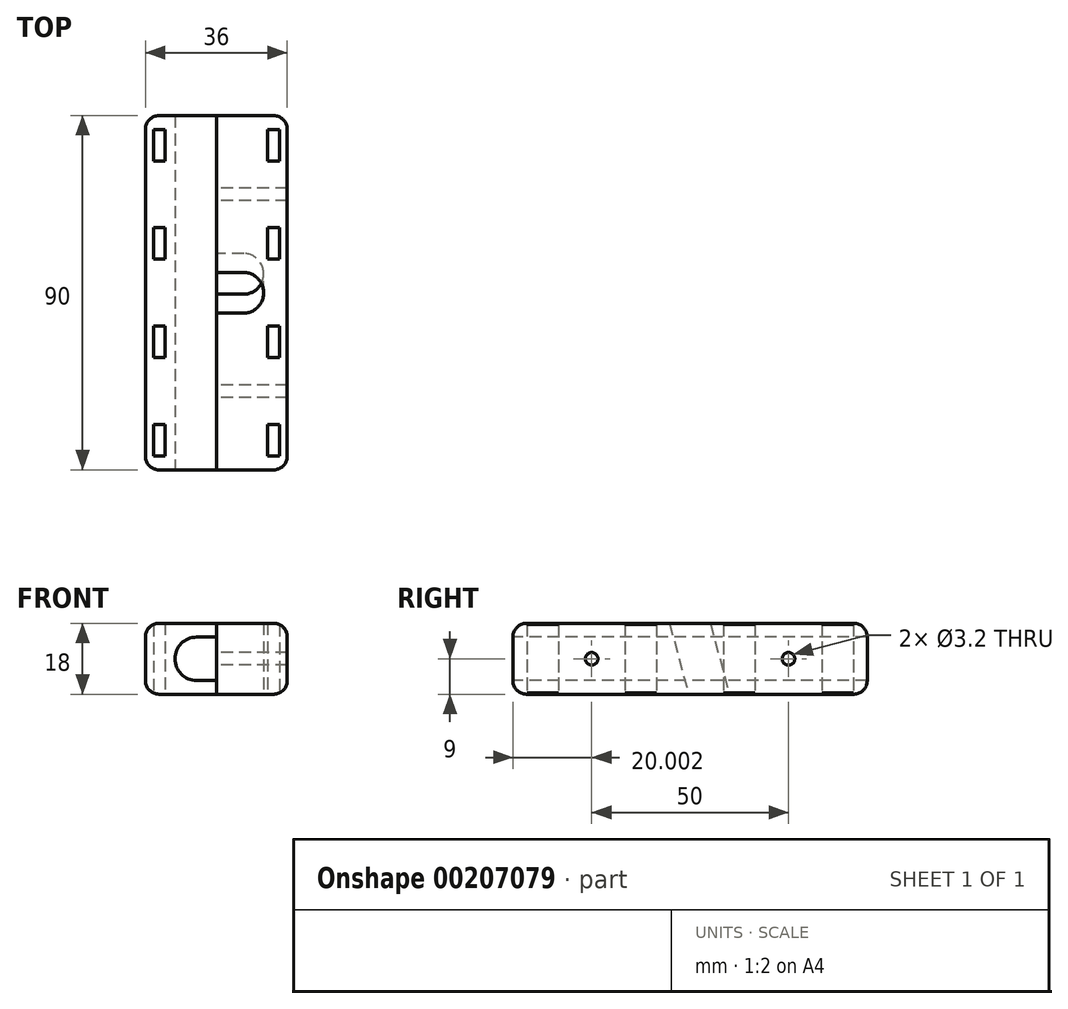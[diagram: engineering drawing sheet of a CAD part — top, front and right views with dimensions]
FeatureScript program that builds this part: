
annotation { "Feature Type Name" : "Feature", "Feature Type Description" : "" }
export const myFeature = defineFeature(function(context is Context, id is Id, definition is map)
    precondition{}
    {
        {
            var Q0;
            Q0=qCreatedBy(makeId("Top.planeOp"),FACE);
            var sketch = newSketch(context, id + "F0", { "sketchPlane" : qUnion([Q0])});
            skLineSegment(sketch, "E0.bottom", {"start": v(1.07, -6.1) * mm, "end": v(19.07, -6.1) * mm});
            skLineSegment(sketch, "E0.top", {"start": v(1.07, 83.9) * mm, "end": v(19.07, 83.9) * mm});
            skLineSegment(sketch, "E0.left", {"start": v(1.07, -6.1) * mm, "end": v(1.07, 83.9) * mm});
            skLineSegment(sketch, "E0.right", {"start": v(19.07, -6.1) * mm, "end": v(19.07, 83.9) * mm});
            skLineSegment(sketch, "E1.bottom", {"start": v(3.07, 80.4) * mm, "end": v(6.07, 80.4) * mm});
            skLineSegment(sketch, "E1.top", {"start": v(3.07, 72.4) * mm, "end": v(6.07, 72.4) * mm});
            skLineSegment(sketch, "E1.left", {"start": v(3.07, 80.4) * mm, "end": v(3.07, 72.4) * mm});
            skLineSegment(sketch, "E1.right", {"start": v(6.07, 80.4) * mm, "end": v(6.07, 72.4) * mm});
            skLineSegment(sketch, "E2.0.1.0", {"start": v(6.07, 55.4) * mm, "end": v(6.07, 47.4) * mm});
            skLineSegment(sketch, "E2.0.1.1", {"start": v(3.07, 55.4) * mm, "end": v(3.07, 47.4) * mm});
            skLineSegment(sketch, "E2.0.1.2", {"start": v(3.07, 47.4) * mm, "end": v(6.07, 47.4) * mm});
            skLineSegment(sketch, "E2.0.1.3", {"start": v(3.07, 55.4) * mm, "end": v(6.07, 55.4) * mm});
            skLineSegment(sketch, "E2.0.2.0", {"start": v(6.07, 30.4) * mm, "end": v(6.07, 22.4) * mm});
            skLineSegment(sketch, "E2.0.2.1", {"start": v(3.07, 30.4) * mm, "end": v(3.07, 22.4) * mm});
            skLineSegment(sketch, "E2.0.2.2", {"start": v(3.07, 22.4) * mm, "end": v(6.07, 22.4) * mm});
            skLineSegment(sketch, "E2.0.2.3", {"start": v(3.07, 30.4) * mm, "end": v(6.07, 30.4) * mm});
            skLineSegment(sketch, "E2.0.3.0", {"start": v(6.07, 5.4) * mm, "end": v(6.07, -2.6) * mm});
            skLineSegment(sketch, "E2.0.3.1", {"start": v(3.07, 5.4) * mm, "end": v(3.07, -2.6) * mm});
            skLineSegment(sketch, "E2.0.3.2", {"start": v(3.07, -2.6) * mm, "end": v(6.07, -2.6) * mm});
            skLineSegment(sketch, "E2.0.3.3", {"start": v(3.07, 5.4) * mm, "end": v(6.07, 5.4) * mm});
            skLineSegment(sketch, "E2.direction1", {"start": v(3.07, 72.4) * mm, "end": v(28.07, 72.4) * mm, "construction": true});
            skLineSegment(sketch, "E2.direction2", {"start": v(3.07, 72.4) * mm, "end": v(3.07, 47.4) * mm, "construction": true});
            skLineSegment(sketch, "E3", {"start": v(6.07, 80.4) * mm, "end": v(6.07, 83.9) * mm, "construction": true});
            skLineSegment(sketch, "E4", {"start": v(6.07, -2.6) * mm, "end": v(6.07, -6.1) * mm, "construction": true});
            skSolve(sketch);
        }
        {
            var Q0;
            Q0 = qSketchRegion(id + "F0", true);
            extrude(context, id + "F1", {"entities" : qUnion([Q0]), "depth" : 18 * mm});
        }
        {
            var Q0;
            Q0=makeQuery(id+"F1.opExtrude","SWEPT_FACE",FACE,{"disambiguationData":[OSD([sQuery(id+"F0.wireOp",EDGE,"E0.bottom")])]});
            var sketch = newSketch(context, id + "F2", { "sketchPlane" : qUnion([Q0])});
            skArc(sketch, "E5", {"start": v(19.07, 11.24) * mm, "mid": v(8.55, 9) * mm, "end": v(19.07, 6.76) * mm});
            skPoint(sketch, "E5.centerSnap0", {"position": v(19.07, 9) * mm});
            skLineSegment(sketch, "E6.bottom", {"start": v(14.05, 3.5) * mm, "end": v(19.07, 3.5) * mm});
            skLineSegment(sketch, "E6.top", {"start": v(14.05, 14.5) * mm, "end": v(19.07, 14.5) * mm});
            skLineSegment(sketch, "E6.left", {"start": v(14.05, 3.5) * mm, "end": v(14.05, 14.5) * mm});
            skLineSegment(sketch, "E6.right", {"start": v(19.07, 3.5) * mm, "end": v(19.07, 14.5) * mm});
            skSolve(sketch);
        }
        {
            var Q0;
            Q0=makeQuery(id+"F1.opExtrude","CAP_EDGE",EDGE,{"disambiguationData":[OSD([sQuery(id+"F0.wireOp",EDGE,"E0.bottom")])],"isStart":false});
            var Q1;
            Q1=makeQuery(id+"F1.opExtrude","CAP_EDGE",EDGE,{"disambiguationData":[OSD([sQuery(id+"F0.wireOp",EDGE,"E0.left")])],"isStart":false});
            var Q2;
            Q2=makeQuery(id+"F1.opExtrude","SWEPT_EDGE",EDGE,{"disambiguationData":[OSD([sQuery(id+"F0.wireOp",EDGE,"E0.bottom"),sQuery(id+"F0.wireOp",EDGE,"E0.left")])]});
            var Q3;
            Q3=makeQuery(id+"F1.opExtrude","CAP_EDGE",EDGE,{"disambiguationData":[OSD([sQuery(id+"F0.wireOp",EDGE,"E0.bottom")])],"isStart":true});
            var Q4;
            Q4=makeQuery(id+"F1.opExtrude","CAP_EDGE",EDGE,{"disambiguationData":[OSD([sQuery(id+"F0.wireOp",EDGE,"E0.left")])],"isStart":true});
            var Q5;
            Q5=makeQuery(id+"F1.opExtrude","SWEPT_EDGE",EDGE,{"disambiguationData":[OSD([sQuery(id+"F0.wireOp",EDGE,"E0.top"),sQuery(id+"F0.wireOp",EDGE,"E0.left")])]});
            var Q6;
            Q6=makeQuery(id+"F1.opExtrude","CAP_EDGE",EDGE,{"disambiguationData":[OSD([sQuery(id+"F0.wireOp",EDGE,"E0.top")])],"isStart":false});
            var Q7;
            Q7=makeQuery(id+"F1.opExtrude","CAP_EDGE",EDGE,{"disambiguationData":[OSD([sQuery(id+"F0.wireOp",EDGE,"E0.top")])],"isStart":true});
            fillet(context, id + "F3", {"entities" : qUnion([Q0, Q1, Q2, Q3, Q4, Q5, Q6, Q7]), "radius" : 3.4 * mm, "tangentPropagation" : true, "allowEdgeOverflow" : false});
        }
        {
            var Q0;
            Q0=makeQuery(id+"F1.opExtrude","SWEPT_BODY",BODY,{"disambiguationData":[OSD([sQuery(id+"F0.wireOp",EDGE,"E0.bottom"),sQuery(id+"F0.wireOp",EDGE,"E0.top"),sQuery(id+"F0.wireOp",EDGE,"E0.left"),sQuery(id+"F0.wireOp",EDGE,"E0.right"),sQuery(id+"F0.wireOp",EDGE,"E1.bottom"),sQuery(id+"F0.wireOp",EDGE,"E1.top"),sQuery(id+"F0.wireOp",EDGE,"E1.left"),sQuery(id+"F0.wireOp",EDGE,"E1.right"),sQuery(id+"F0.wireOp",EDGE,"E2.0.1.0"),sQuery(id+"F0.wireOp",EDGE,"E2.0.1.1"),sQuery(id+"F0.wireOp",EDGE,"E2.0.1.2"),sQuery(id+"F0.wireOp",EDGE,"E2.0.1.3"),sQuery(id+"F0.wireOp",EDGE,"E2.0.2.0"),sQuery(id+"F0.wireOp",EDGE,"E2.0.2.1"),sQuery(id+"F0.wireOp",EDGE,"E2.0.2.2"),sQuery(id+"F0.wireOp",EDGE,"E2.0.2.3"),sQuery(id+"F0.wireOp",EDGE,"E2.0.3.0"),sQuery(id+"F0.wireOp",EDGE,"E2.0.3.1"),sQuery(id+"F0.wireOp",EDGE,"E2.0.3.2"),sQuery(id+"F0.wireOp",EDGE,"E2.0.3.3")])]});
            var Q1;
            Q1=makeQuery(id+"F1.opExtrude","SWEPT_FACE",FACE,{"disambiguationData":[OSD([sQuery(id+"F0.wireOp",EDGE,"E0.right")])]});
            mirror(context, id + "F4", {"entities" : qUnion([Q0]), "mirrorPlane" : qUnion([Q1])});
        }
        {
            var Q0;
            Q0 = qSketchRegion(id + "F2", true);
            extrude(context, id + "F5", {"entities" : qUnion([Q0]), "operationType" : NewBodyOperationType.REMOVE, "endBound" : BoundingType.THROUGH_ALL, "oppositeDirection" : true, "depth" : 25 * mm});
        }
        {
            var Q0;
            Q0=makeQuery(id+"F4.opPattern","COPY",FACE,{"derivedFrom":makeQuery(id+"F1.opExtrude","SWEPT_FACE",FACE,{"disambiguationData":[OSD([sQuery(id+"F0.wireOp",EDGE,"E0.right")])]}),"instanceName":"1"});
            var sketch = newSketch(context, id + "F6", { "sketchPlane" : qUnion([Q0])});
            skLineSegment(sketch, "E7", {"start": v(-3.85, -6.17) * mm, "end": v(-45.34, -6.17) * mm, "construction": true});
            skLineSegment(sketch, "E8", {"start": v(-45.34, -6.17) * mm, "end": v(-32.5, 41.73) * mm, "construction": true});
            skLineSegment(sketch, "E9.bottom", {"start": v(-32.97, 20.67) * mm, "end": v(-42.63, 23.26) * mm});
            skLineSegment(sketch, "E9.top", {"start": v(-39.88, -5.09) * mm, "end": v(-49.54, -2.5) * mm});
            skLineSegment(sketch, "E9.left", {"start": v(-32.97, 20.67) * mm, "end": v(-39.88, -5.09) * mm});
            skLineSegment(sketch, "E9.right", {"start": v(-42.63, 23.26) * mm, "end": v(-49.54, -2.5) * mm});
            skLineSegment(sketch, "E10", {"start": v(-37.8, 21.97) * mm, "end": v(-36.5, 26.85) * mm, "construction": true});
            skSolve(sketch);
        }
        {
            var Q0;
            Q0 = qSketchRegion(id + "F6", true);
            extrude(context, id + "F7", {"entities" : qUnion([Q0]), "operationType" : NewBodyOperationType.REMOVE, "oppositeDirection" : true, "depth" : 12 * mm});
        }
        {
            var Q0;
            Q0=makeQuery(id+"F7.boolean.opBoolean","COPY",EDGE,{"derivedFrom":makeQuery(id+"F7.opExtrude","CAP_EDGE",EDGE,{"disambiguationData":[OSD([sQuery(id+"F6.wireOp",EDGE,"E9.right")])],"isStart":false})});
            var Q1;
            Q1=makeQuery(id+"F7.boolean.opBoolean","COPY",EDGE,{"derivedFrom":makeQuery(id+"F7.opExtrude","CAP_EDGE",EDGE,{"disambiguationData":[OSD([sQuery(id+"F6.wireOp",EDGE,"E9.left")])],"isStart":false})});
            fillet(context, id + "F8", {"entities" : qUnion([Q0, Q1]), "radius" : 5 * mm, "tangentPropagation" : true, "allowEdgeOverflow" : false});
        }
        {
            var Q0;
            {var subQ16=sQuery(id+"F0.wireOp",EDGE,"E0.right");var subQ18=sQuery(id+"F0.wireOp",EDGE,"E0.top");Q0=makeQuery(id+"F7.boolean.opBoolean","SPLIT",FACE,{"disambiguationData":[TD([makeQuery(id+"F4.opPattern","COPY",FACE,{"derivedFrom":makeQuery(id+"F1.opExtrude","SWEPT_FACE",FACE,{"disambiguationData":[OSD([subQ18])]}),"instanceName":"1"})])],"derivedFrom":makeQuery(id+"F4.opPattern","COPY",FACE,{"derivedFrom":makeQuery(id+"F1.opExtrude","SWEPT_FACE",FACE,{"disambiguationData":[OSD([subQ16])]}),"instanceName":"1"})});}
            var sketch = newSketch(context, id + "F9", { "sketchPlane" : qUnion([Q0])});
            skCircle(sketch, "E11", {"center": v(-63.9, 9) * mm, "radius": 1.6 * mm});
            skPoint(sketch, "E11.centerSnap0", {"position": v(-83.9, 9) * mm});
            skLineSegment(sketch, "E12", {"start": v(-83.9, 9) * mm, "end": v(-63.9, 9) * mm, "construction": true});
            skCircle(sketch, "E13", {"center": v(-13.9, 9) * mm, "radius": 1.6 * mm});
            skLineSegment(sketch, "E14", {"start": v(-13.9, 9) * mm, "end": v(6.1, 9) * mm, "construction": true});
            skLineSegment(sketch, "E15", {"start": v(-72.4, 13) * mm, "end": v(-55.4, 13) * mm, "construction": true});
            skLineSegment(sketch, "E16", {"start": v(-72.4, 13) * mm, "end": v(-63.9, 13) * mm, "construction": true});
            skSolve(sketch);
        }
        {
            var Q0;
            Q0 = qSketchRegion(id + "F9", true);
            extrude(context, id + "F10", {"entities" : qUnion([Q0]), "operationType" : NewBodyOperationType.REMOVE, "endBound" : BoundingType.THROUGH_ALL, "oppositeDirection" : true, "depth" : 25 * mm});
        }
    });
